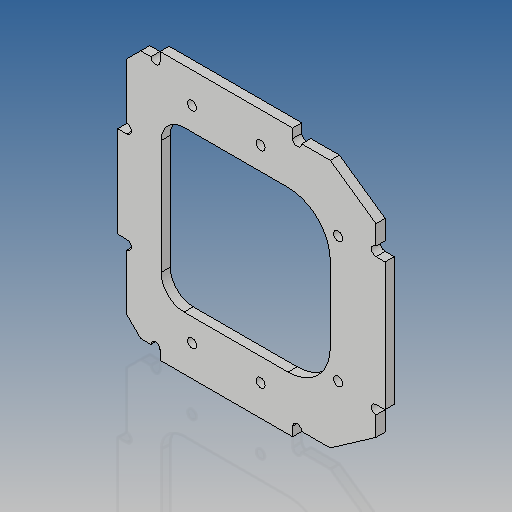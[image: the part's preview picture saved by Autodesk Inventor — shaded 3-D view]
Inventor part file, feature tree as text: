
AUTODESK INVENTOR PART (.ipt)
format: ipt  version: 2017 (Build 210142000, 142)  size: 175,616 bytes
history: native  units: mm
features: reference x9, other x5, extrude x1, sketch x1
ambient origin geometry x8: Origin, YZ Plane, XZ Plane, XY Plane, X Axis, Y Axis, Z Axis, Center Point
bodies: Body1 (feature_tree)
feature tree (16):
  other  "Sólido1"
  extrude  "Extrusión1"  Depth=40.0mm
  sketch  "Boceto1"  dims[d0=109.0mm d1=40.0mm d2=2.0mm d3=109.0mm d7=4.0mm d8=6.0mm d9=6.0mm d10=14.0mm d11=20.0mm d12=14.0mm d13=20.0mm d14=6.0mm d15=6.0mm d16=20.0mm d17=10.0mm d18=4.0mm d19=0.0mm d20=58.0mm d21=3.0mm d22=3.0mm d23=15.0mm d24=4.0mm d25=3.0mm d26=4.0mm d27=70.0mm]
  reference  "Referencia1"
  reference  "Referencia2"
  reference  "Referencia3"
  reference  "Referencia4"
  reference  "Referencia5"
  reference  "Referencia6"
  reference  "Referencia7"
  reference  "Referencia8"
  reference  "Referencia9"
  other  "<userpath>\Documents\GitHub\actor-re-actor\models\inventor-caja\Case\Case-D.iam"
  other  "Case-D.iam"
  other  "Carcasa:1"
  other  "<userpath>\Documents\GitHub\actor-re-actor\models\inventor-caja\Case\Case-D.iam"
